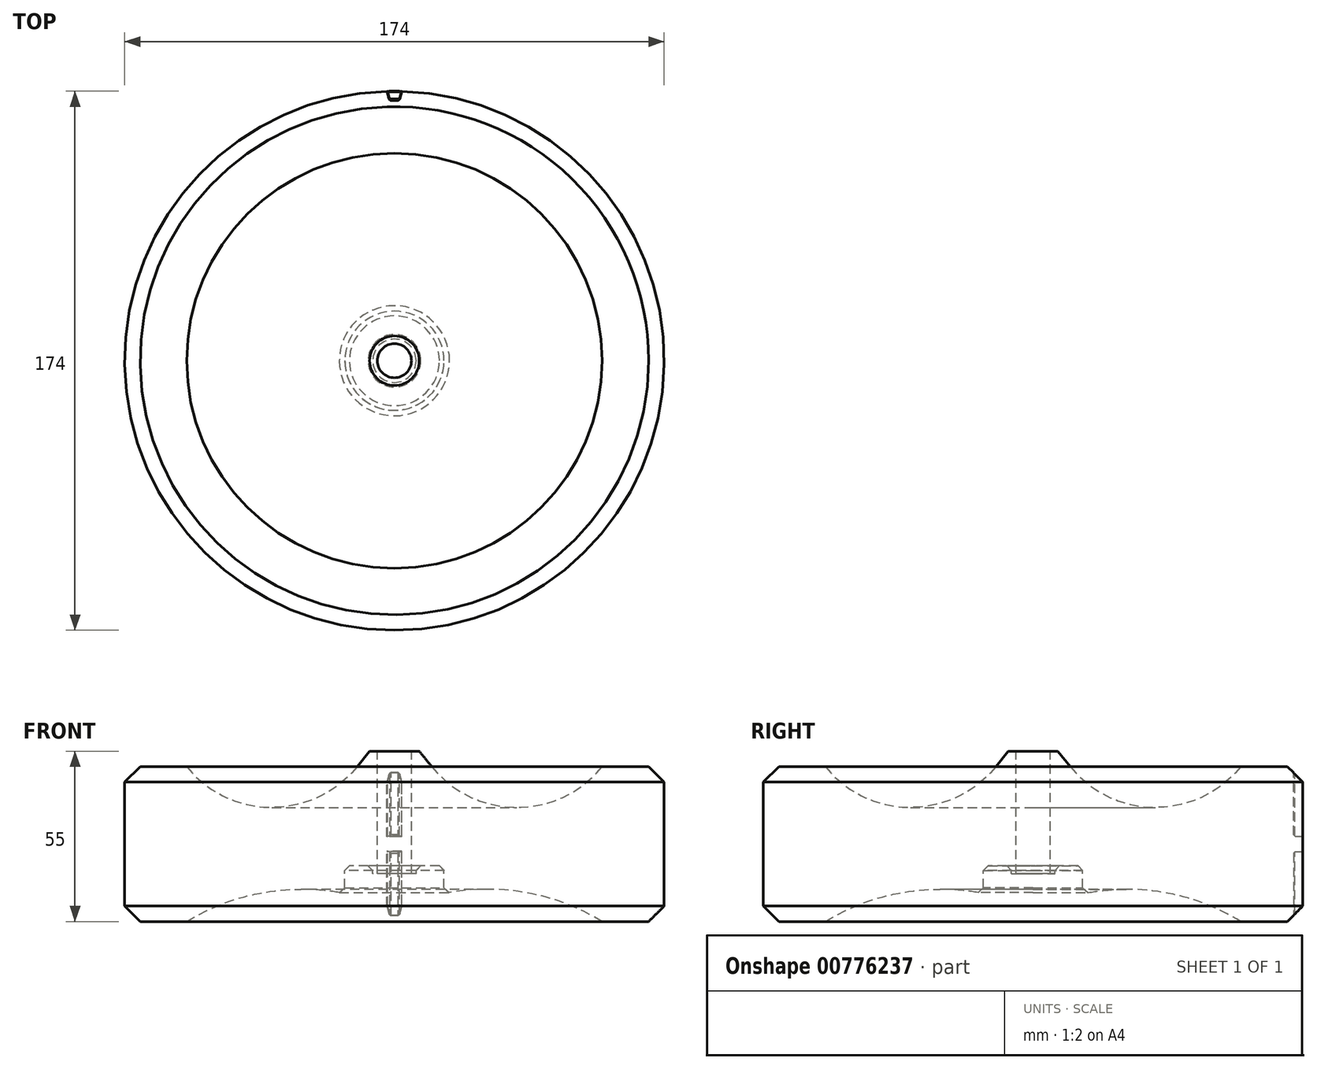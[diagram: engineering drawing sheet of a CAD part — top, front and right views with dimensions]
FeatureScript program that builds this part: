
annotation { "Feature Type Name" : "Feature", "Feature Type Description" : "" }
export const myFeature = defineFeature(function(context is Context, id is Id, definition is map)
    precondition{}
    {
        {
            var Q0;
            Q0=qCreatedBy(makeId("Front.planeOp"),FACE);
            var sketch = newSketch(context, id + "F0", { "sketchPlane" : qUnion([Q0])});
            skLineSegment(sketch, "E0.bottom", {"start": v(0, 0) * mm, "end": v(87, 0) * mm});
            skLineSegment(sketch, "E0.top", {"start": v(0, 50) * mm, "end": v(87, 50) * mm});
            skLineSegment(sketch, "E0.left", {"start": v(0, 0) * mm, "end": v(0, 50) * mm});
            skLineSegment(sketch, "E0.right", {"start": v(87, 0) * mm, "end": v(87, 50) * mm});
            skLineSegment(sketch, "E1", {"start": v(0, 50) * mm, "end": v(0, 55) * mm});
            skLineSegment(sketch, "E2", {"start": v(0, 55) * mm, "end": v(0, 18) * mm});
            skLineSegment(sketch, "E3", {"start": v(0, 18) * mm, "end": v(16, 18) * mm});
            skLineSegment(sketch, "E4", {"start": v(16, 18) * mm, "end": v(16, 0) * mm});
            skLineSegment(sketch, "E5.bottom", {"start": v(0, 55) * mm, "end": v(5.5, 55) * mm});
            skLineSegment(sketch, "E5.top", {"start": v(0, 0) * mm, "end": v(5.5, 0) * mm});
            skLineSegment(sketch, "E5.left", {"start": v(0, 55) * mm, "end": v(0, 0) * mm});
            skLineSegment(sketch, "E5.right", {"start": v(5.5, 55) * mm, "end": v(5.5, 0) * mm});
            skLineSegment(sketch, "E6", {"start": v(5.5, 55) * mm, "end": v(8, 55) * mm});
            skLineSegment(sketch, "E7", {"start": v(8, 55) * mm, "end": v(12.02, 50) * mm});
            skLineSegment(sketch, "E8", {"start": v(0, 18) * mm, "end": v(0, 15.5) * mm});
            skLineSegment(sketch, "E9", {"start": v(0, 15.5) * mm, "end": v(7, 15.5) * mm});
            skLineSegment(sketch, "E10", {"start": v(7, 15.5) * mm, "end": v(7, 18) * mm});
            skLineSegment(sketch, "E11", {"start": v(87, 50) * mm, "end": v(67, 50) * mm});
            skArc(sketch, "E12", {"start": v(12.02, 50) * mm, "mid": v(39.51, 36.84) * mm, "end": v(67, 50) * mm});
            skLineSegment(sketch, "E13", {"start": v(87, 0) * mm, "end": v(67, 0) * mm});
            skArc(sketch, "E14", {"start": v(67, 0) * mm, "mid": v(42.35, 9.34) * mm, "end": v(16, 9) * mm});
            skSolve(sketch);
        }
        {
            var Q0;
            {var subQ0=sQuery(id+"F0.wireOp",EDGE,"E0.right");Q0=makeQuery(id+"F0.imprint","IMPRINT",FACE,{"disambiguationData":[TD([[makeQuery(id+"F0.imprint","IMPRINT",EDGE,{"derivedFrom":subQ0}),1.0]])]});}
            var Q1;
            {var subQ4=sQuery(id+"F0.wireOp",EDGE,"E6");Q1=makeQuery(id+"F0.imprint","IMPRINT",FACE,{"disambiguationData":[TD([[makeQuery(id+"F0.imprint","IMPRINT",EDGE,{"derivedFrom":subQ4}),-1.0]])]});}
            var Q2;
            {var subQ0=sQuery(id+"F0.wireOp",EDGE,"E10");Q2=makeQuery(id+"F0.imprint","IMPRINT",FACE,{"disambiguationData":[TD([[makeQuery(id+"F0.imprint","IMPRINT",EDGE,{"derivedFrom":subQ0}),1.0]])]});}
            var Q3;
            Q3=sQuery(id+"F0.wireOp",EDGE,"E5.left");
            revolve(context, id + "F1", {"surfaceOperationType" : NewSurfaceOperationType.NEW, "entities" : qUnion([Q0, Q1, Q2]), "axis" : qUnion([Q3]), "revolveType" : RevolveType.FULL});
        }
        {
            var Q0;
            Q0=makeQuery(id+"F1.opRevolve","SWEPT_EDGE",EDGE,{"disambiguationData":[OSD([sQuery(id+"F0.wireOp",EDGE,"E0.top"),sQuery(id+"F0.wireOp",EDGE,"E0.right")])]});
            var Q1;
            Q1=makeQuery(id+"F1.opRevolve","SWEPT_EDGE",EDGE,{"disambiguationData":[OSD([sQuery(id+"F0.wireOp",EDGE,"E0.bottom"),sQuery(id+"F0.wireOp",EDGE,"E0.right")])]});
            chamfer(context, id + "F2", {"entities" : qUnion([Q0, Q1]), "width" : 5 * mm, "tangentPropagation" : true});
        }
        {
            var Q0;
            Q0=makeQuery(id+"F1.opRevolve","SWEPT_FACE",FACE,{"disambiguationData":[OSD([sQuery(id+"F0.wireOp",EDGE,"E0.top")])]});
            var sketch = newSketch(context, id + "F3", { "sketchPlane" : qUnion([Q0])});
            skLineSegment(sketch, "E15", {"start": v(0, 0) * mm, "end": v(0, 87) * mm});
            skLineSegment(sketch, "E16.bottom", {"start": v(0, 87) * mm, "end": v(1.5, 87) * mm});
            skLineSegment(sketch, "E16.top", {"start": v(0, 84) * mm, "end": v(1.5, 84) * mm});
            skLineSegment(sketch, "E16.left", {"start": v(0, 87) * mm, "end": v(0, 84) * mm});
            skLineSegment(sketch, "E16.right", {"start": v(1.5, 87) * mm, "end": v(1.5, 84) * mm});
            skLineSegment(sketch, "E17", {"start": v(1.5, 84) * mm, "end": v(2.76, 88.68) * mm});
            skLineSegment(sketch, "E18.MirrorCS", {"start": v(-1.5, 84) * mm, "end": v(-2.76, 88.68) * mm});
            skLineSegment(sketch, "E19.MirrorCS", {"start": v(-1.5, 87) * mm, "end": v(-1.5, 84) * mm});
            skLineSegment(sketch, "E20.MirrorCS", {"start": v(0, 84) * mm, "end": v(-1.5, 84) * mm});
            skLineSegment(sketch, "E21.MirrorCS", {"start": v(0, 87) * mm, "end": v(-1.5, 87) * mm});
            skLineSegment(sketch, "E22", {"start": v(-2.76, 88.68) * mm, "end": v(2.76, 88.68) * mm});
            skSolve(sketch);
        }
        {
            var Q0;
            {var subQ0=sQuery(id+"F3.wireOp",EDGE,"E16.bottom");Q0=makeQuery(id+"F3.imprint","IMPRINT",FACE,{"disambiguationData":[TD([[makeQuery(id+"F3.imprint","IMPRINT",EDGE,{"derivedFrom":subQ0}),-1.0]])]});}
            var Q1;
            {var subQ0=sQuery(id+"F3.wireOp",EDGE,"E21.MirrorCS");Q1=makeQuery(id+"F3.imprint","IMPRINT",FACE,{"disambiguationData":[TD([[makeQuery(id+"F3.imprint","IMPRINT",EDGE,{"derivedFrom":subQ0}),1.0]])]});}
            var Q2;
            {var subQ0=sQuery(id+"F3.wireOp",EDGE,"E16.top");Q2=makeQuery(id+"F3.imprint","IMPRINT",FACE,{"disambiguationData":[TD([[makeQuery(id+"F3.imprint","IMPRINT",EDGE,{"derivedFrom":subQ0}),1.0]])]});}
            var Q3;
            {var subQ0=sQuery(id+"F3.wireOp",EDGE,"E19.MirrorCS");var subQ1=sQuery(id+"F3.wireOp",EDGE,"E18.MirrorCS");var subQ2=makeQuery(id+"F3.imprint","INTERSECT",VERTEX,{"derivedFrom":[subQ1,subQ0,sQuery(id+"F3.wireOp",EDGE,"E20.MirrorCS")]});Q3=makeQuery(id+"F3.imprint","IMPRINT",FACE,{"disambiguationData":[TD([[makeQuery(id+"F3.imprint","IMPRINT",EDGE,{"disambiguationData":[TD([[subQ2,-1.0]])],"derivedFrom":subQ1}),-1.0]])]});}
            var Q4;
            {var subQ0=sQuery(id+"F3.wireOp",EDGE,"E16.left");Q4=makeQuery(id+"F3.imprint","IMPRINT",FACE,{"disambiguationData":[TD([[makeQuery(id+"F3.imprint","IMPRINT",EDGE,{"derivedFrom":subQ0}),-1.0]])]});}
            var Q5;
            {var subQ0=sQuery(id+"F3.wireOp",EDGE,"E17");var subQ1=sQuery(id+"F3.wireOp",EDGE,"E16.right");var subQ2=makeQuery(id+"F3.imprint","INTERSECT",VERTEX,{"derivedFrom":[sQuery(id+"F3.wireOp",EDGE,"E16.top"),subQ1,subQ0]});Q5=makeQuery(id+"F3.imprint","IMPRINT",FACE,{"disambiguationData":[TD([[makeQuery(id+"F3.imprint","IMPRINT",EDGE,{"disambiguationData":[TD([[subQ2,1.0]])],"derivedFrom":subQ1}),1.0]])]});}
            extrude(context, id + "F4", {"entities" : qUnion([Q0, Q1, Q2, Q3, Q4, Q5]), "operationType" : NewBodyOperationType.REMOVE, "oppositeDirection" : true, "depth" : 22.5 * mm, "offsetDistance" : 25 * mm});
        }
        {
            var Q0;
            Q0 = qSketchRegion(id + "F3", true);
            extrude(context, id + "F5", {"entities" : qUnion([Q0]), "operationType" : NewBodyOperationType.REMOVE, "oppositeDirection" : true, "depth" : 75.5 * mm, "offsetDistance" : 25 * mm, "hasSecondDirection" : true, "secondDirectionOppositeDirection" : true, "secondDirectionDepth" : 27.5 * mm});
        }
        {
            var Q0;
            Q0=makeQuery(id+"F4.boolean.opBoolean","COPY",EDGE,{"derivedFrom":makeQuery(id+"F4.opExtrude","CAP_EDGE",EDGE,{"disambiguationData":[OSD([sQuery(id+"F3.wireOp",EDGE,"E16.top"),sQuery(id+"F3.wireOp",EDGE,"E20.MirrorCS")])],"isStart":false})});
            var Q1;
            Q1=makeQuery(id+"F4.boolean.opBoolean","COPY",EDGE,{"derivedFrom":makeQuery(id+"F4.opExtrude","SWEPT_EDGE",EDGE,{"disambiguationData":[OSD([sQuery(id+"F3.wireOp",EDGE,"E16.top"),sQuery(id+"F3.wireOp",EDGE,"E16.right"),sQuery(id+"F3.wireOp",EDGE,"E17")])]})});
            var Q2;
            Q2=makeQuery(id+"F4.boolean.opBoolean","COPY",EDGE,{"derivedFrom":makeQuery(id+"F4.opExtrude","SWEPT_EDGE",EDGE,{"disambiguationData":[OSD([sQuery(id+"F3.wireOp",EDGE,"E18.MirrorCS"),sQuery(id+"F3.wireOp",EDGE,"E19.MirrorCS"),sQuery(id+"F3.wireOp",EDGE,"E20.MirrorCS")])]})});
            var Q3;
            Q3=makeQuery(id+"F5.boolean.opBoolean","COPY",EDGE,{"derivedFrom":makeQuery(id+"F5.opExtrude","SWEPT_EDGE",EDGE,{"disambiguationData":[OSD([sQuery(id+"F3.wireOp",EDGE,"E16.top"),sQuery(id+"F3.wireOp",EDGE,"E16.right"),sQuery(id+"F3.wireOp",EDGE,"E17")])]})});
            var Q4;
            Q4=makeQuery(id+"F5.boolean.opBoolean","COPY",EDGE,{"derivedFrom":makeQuery(id+"F5.opExtrude","SWEPT_EDGE",EDGE,{"disambiguationData":[OSD([sQuery(id+"F3.wireOp",EDGE,"E18.MirrorCS"),sQuery(id+"F3.wireOp",EDGE,"E19.MirrorCS"),sQuery(id+"F3.wireOp",EDGE,"E20.MirrorCS")])]})});
            var Q5;
            Q5=makeQuery(id+"F5.boolean.opBoolean","COPY",EDGE,{"derivedFrom":makeQuery(id+"F5.opExtrude","CAP_EDGE",EDGE,{"disambiguationData":[OSD([sQuery(id+"F3.wireOp",EDGE,"E16.top"),sQuery(id+"F3.wireOp",EDGE,"E20.MirrorCS")])],"isStart":true})});
            chamfer(context, id + "F6", {"entities" : qUnion([Q0, Q1, Q2, Q3, Q4, Q5]), "width" : .5 * mm, "tangentPropagation" : true});
        }
        {
            var Q0;
            Q0=makeQuery(id+"F4.boolean.opBoolean","INTERSECT",EDGE,{"derivedFrom":[makeQuery(id+"F1.opRevolve","SWEPT_FACE",FACE,{"disambiguationData":[OSD([sQuery(id+"F0.wireOp",EDGE,"E0.right")])]}),makeQuery(id+"F4.opExtrude","SWEPT_FACE",FACE,{"disambiguationData":[OSD([sQuery(id+"F3.wireOp",EDGE,"E17")])]})]});
            var Q1;
            Q1=makeQuery(id+"F4.boolean.opBoolean","INTERSECT",EDGE,{"derivedFrom":[makeQuery(id+"F1.opRevolve","SWEPT_FACE",FACE,{"disambiguationData":[OSD([sQuery(id+"F0.wireOp",EDGE,"E0.right")])]}),makeQuery(id+"F4.opExtrude","CAP_FACE",FACE,{"disambiguationData":[OSD([sQuery(id+"F3.wireOp",EDGE,"E16.top"),sQuery(id+"F3.wireOp",EDGE,"E17"),sQuery(id+"F3.wireOp",EDGE,"E18.MirrorCS"),sQuery(id+"F3.wireOp",EDGE,"E20.MirrorCS"),sQuery(id+"F3.wireOp",EDGE,"E22")])],"isStart":false})]});
            var Q2;
            Q2=makeQuery(id+"F4.boolean.opBoolean","INTERSECT",EDGE,{"derivedFrom":[makeQuery(id+"F1.opRevolve","SWEPT_FACE",FACE,{"disambiguationData":[OSD([sQuery(id+"F0.wireOp",EDGE,"E0.right")])]}),makeQuery(id+"F4.opExtrude","SWEPT_FACE",FACE,{"disambiguationData":[OSD([sQuery(id+"F3.wireOp",EDGE,"E18.MirrorCS")])]})]});
            var Q3;
            Q3=makeQuery(id+"F5.boolean.opBoolean","INTERSECT",EDGE,{"derivedFrom":[makeQuery(id+"F1.opRevolve","SWEPT_FACE",FACE,{"disambiguationData":[OSD([sQuery(id+"F0.wireOp",EDGE,"E0.right")])]}),makeQuery(id+"F5.opExtrude","SWEPT_FACE",FACE,{"disambiguationData":[OSD([sQuery(id+"F3.wireOp",EDGE,"E18.MirrorCS")])]})]});
            var Q4;
            Q4=makeQuery(id+"F5.boolean.opBoolean","INTERSECT",EDGE,{"derivedFrom":[makeQuery(id+"F1.opRevolve","SWEPT_FACE",FACE,{"disambiguationData":[OSD([sQuery(id+"F0.wireOp",EDGE,"E0.right")])]}),makeQuery(id+"F5.opExtrude","CAP_FACE",FACE,{"disambiguationData":[OSD([sQuery(id+"F3.wireOp",EDGE,"E16.top"),sQuery(id+"F3.wireOp",EDGE,"E17"),sQuery(id+"F3.wireOp",EDGE,"E18.MirrorCS"),sQuery(id+"F3.wireOp",EDGE,"E20.MirrorCS"),sQuery(id+"F3.wireOp",EDGE,"E22")])],"isStart":true})]});
            var Q5;
            Q5=makeQuery(id+"F5.boolean.opBoolean","INTERSECT",EDGE,{"derivedFrom":[makeQuery(id+"F1.opRevolve","SWEPT_FACE",FACE,{"disambiguationData":[OSD([sQuery(id+"F0.wireOp",EDGE,"E0.right")])]}),makeQuery(id+"F5.opExtrude","SWEPT_FACE",FACE,{"disambiguationData":[OSD([sQuery(id+"F3.wireOp",EDGE,"E17")])]})]});
            var Q6;
            Q6=makeQuery(id+"F4.boolean.opBoolean","INTERSECT",EDGE,{"derivedFrom":[makeQuery(id+"F2.opChamfer","BLEND_FACE",FACE,{"disambiguationData":[OSD([sQuery(id+"F0.wireOp",EDGE,"E0.right"),sQuery(id+"F0.wireOp",EDGE,"E11")])]}),makeQuery(id+"F4.opExtrude","SWEPT_FACE",FACE,{"disambiguationData":[OSD([sQuery(id+"F3.wireOp",EDGE,"E17")])]})]});
            var Q7;
            Q7=makeQuery(id+"F6.opChamfer","BLEND_EDGE",EDGE,{"blendedFrom":[makeQuery(id+"F4.boolean.opBoolean","COPY",EDGE,{"derivedFrom":makeQuery(id+"F4.opExtrude","SWEPT_EDGE",EDGE,{"disambiguationData":[OSD([sQuery(id+"F3.wireOp",EDGE,"E16.top"),sQuery(id+"F3.wireOp",EDGE,"E16.right"),sQuery(id+"F3.wireOp",EDGE,"E17")])]})}),makeQuery(id+"F2.opChamfer","BLEND_FACE",FACE,{"disambiguationData":[OSD([sQuery(id+"F0.wireOp",EDGE,"E0.right"),sQuery(id+"F0.wireOp",EDGE,"E11")])]})],"blendedInto":[makeQuery(id+"F2.opChamfer","BLEND_FACE",FACE,{"disambiguationData":[OSD([sQuery(id+"F0.wireOp",EDGE,"E0.right"),sQuery(id+"F0.wireOp",EDGE,"E11")])]})]});
            var Q8;
            Q8=makeQuery(id+"F4.boolean.opBoolean","INTERSECT",EDGE,{"derivedFrom":[makeQuery(id+"F2.opChamfer","BLEND_FACE",FACE,{"disambiguationData":[OSD([sQuery(id+"F0.wireOp",EDGE,"E0.right"),sQuery(id+"F0.wireOp",EDGE,"E11")])]}),makeQuery(id+"F4.opExtrude","SWEPT_FACE",FACE,{"disambiguationData":[OSD([sQuery(id+"F3.wireOp",EDGE,"E16.top"),sQuery(id+"F3.wireOp",EDGE,"E20.MirrorCS")])]})]});
            var Q9;
            Q9=makeQuery(id+"F6.opChamfer","BLEND_EDGE",EDGE,{"blendedFrom":[makeQuery(id+"F4.boolean.opBoolean","COPY",EDGE,{"derivedFrom":makeQuery(id+"F4.opExtrude","SWEPT_EDGE",EDGE,{"disambiguationData":[OSD([sQuery(id+"F3.wireOp",EDGE,"E18.MirrorCS"),sQuery(id+"F3.wireOp",EDGE,"E19.MirrorCS"),sQuery(id+"F3.wireOp",EDGE,"E20.MirrorCS")])]})}),makeQuery(id+"F2.opChamfer","BLEND_FACE",FACE,{"disambiguationData":[OSD([sQuery(id+"F0.wireOp",EDGE,"E0.right"),sQuery(id+"F0.wireOp",EDGE,"E11")])]})],"blendedInto":[makeQuery(id+"F2.opChamfer","BLEND_FACE",FACE,{"disambiguationData":[OSD([sQuery(id+"F0.wireOp",EDGE,"E0.right"),sQuery(id+"F0.wireOp",EDGE,"E11")])]})]});
            var Q10;
            Q10=makeQuery(id+"F5.boolean.opBoolean","INTERSECT",EDGE,{"derivedFrom":[makeQuery(id+"F2.opChamfer","BLEND_FACE",FACE,{"disambiguationData":[OSD([sQuery(id+"F0.wireOp",EDGE,"E0.right"),sQuery(id+"F0.wireOp",EDGE,"E13")])]}),makeQuery(id+"F5.opExtrude","SWEPT_FACE",FACE,{"disambiguationData":[OSD([sQuery(id+"F3.wireOp",EDGE,"E18.MirrorCS")])]})]});
            var Q11;
            Q11=makeQuery(id+"F6.opChamfer","BLEND_EDGE",EDGE,{"blendedFrom":[makeQuery(id+"F5.boolean.opBoolean","COPY",EDGE,{"derivedFrom":makeQuery(id+"F5.opExtrude","SWEPT_EDGE",EDGE,{"disambiguationData":[OSD([sQuery(id+"F3.wireOp",EDGE,"E18.MirrorCS"),sQuery(id+"F3.wireOp",EDGE,"E19.MirrorCS"),sQuery(id+"F3.wireOp",EDGE,"E20.MirrorCS")])]})}),makeQuery(id+"F2.opChamfer","BLEND_FACE",FACE,{"disambiguationData":[OSD([sQuery(id+"F0.wireOp",EDGE,"E0.right"),sQuery(id+"F0.wireOp",EDGE,"E13")])]})],"blendedInto":[makeQuery(id+"F2.opChamfer","BLEND_FACE",FACE,{"disambiguationData":[OSD([sQuery(id+"F0.wireOp",EDGE,"E0.right"),sQuery(id+"F0.wireOp",EDGE,"E13")])]})]});
            var Q12;
            Q12=makeQuery(id+"F5.boolean.opBoolean","INTERSECT",EDGE,{"derivedFrom":[makeQuery(id+"F2.opChamfer","BLEND_FACE",FACE,{"disambiguationData":[OSD([sQuery(id+"F0.wireOp",EDGE,"E0.right"),sQuery(id+"F0.wireOp",EDGE,"E13")])]}),makeQuery(id+"F5.opExtrude","SWEPT_FACE",FACE,{"disambiguationData":[OSD([sQuery(id+"F3.wireOp",EDGE,"E16.top"),sQuery(id+"F3.wireOp",EDGE,"E20.MirrorCS")])]})]});
            var Q13;
            Q13=makeQuery(id+"F6.opChamfer","BLEND_EDGE",EDGE,{"blendedFrom":[makeQuery(id+"F5.boolean.opBoolean","COPY",EDGE,{"derivedFrom":makeQuery(id+"F5.opExtrude","SWEPT_EDGE",EDGE,{"disambiguationData":[OSD([sQuery(id+"F3.wireOp",EDGE,"E16.top"),sQuery(id+"F3.wireOp",EDGE,"E16.right"),sQuery(id+"F3.wireOp",EDGE,"E17")])]})}),makeQuery(id+"F2.opChamfer","BLEND_FACE",FACE,{"disambiguationData":[OSD([sQuery(id+"F0.wireOp",EDGE,"E0.right"),sQuery(id+"F0.wireOp",EDGE,"E13")])]})],"blendedInto":[makeQuery(id+"F2.opChamfer","BLEND_FACE",FACE,{"disambiguationData":[OSD([sQuery(id+"F0.wireOp",EDGE,"E0.right"),sQuery(id+"F0.wireOp",EDGE,"E13")])]})]});
            var Q14;
            Q14=makeQuery(id+"F5.boolean.opBoolean","INTERSECT",EDGE,{"derivedFrom":[makeQuery(id+"F2.opChamfer","BLEND_FACE",FACE,{"disambiguationData":[OSD([sQuery(id+"F0.wireOp",EDGE,"E0.right"),sQuery(id+"F0.wireOp",EDGE,"E13")])]}),makeQuery(id+"F5.opExtrude","SWEPT_FACE",FACE,{"disambiguationData":[OSD([sQuery(id+"F3.wireOp",EDGE,"E17")])]})]});
            var Q15;
            Q15=makeQuery(id+"F4.boolean.opBoolean","INTERSECT",EDGE,{"derivedFrom":[makeQuery(id+"F2.opChamfer","BLEND_FACE",FACE,{"disambiguationData":[OSD([sQuery(id+"F0.wireOp",EDGE,"E0.right"),sQuery(id+"F0.wireOp",EDGE,"E11")])]}),makeQuery(id+"F4.opExtrude","SWEPT_FACE",FACE,{"disambiguationData":[OSD([sQuery(id+"F3.wireOp",EDGE,"E18.MirrorCS")])]})]});
            chamfer(context, id + "F7", {"entities" : qUnion([Q0, Q1, Q2, Q3, Q4, Q5, Q6, Q7, Q8, Q9, Q10, Q11, Q12, Q13, Q14, Q15]), "width" : .15 * mm, "tangentPropagation" : true});
        }
        {
            var Q0;
            Q0=makeQuery(id+"F1.opRevolve","SWEPT_EDGE",EDGE,{"disambiguationData":[OSD([sQuery(id+"F0.wireOp",EDGE,"E4"),sQuery(id+"F0.wireOp",EDGE,"E14")])]});
            var Q1;
            Q1=makeQuery(id+"F1.opRevolve","SWEPT_EDGE",EDGE,{"disambiguationData":[OSD([sQuery(id+"F0.wireOp",EDGE,"E3"),sQuery(id+"F0.wireOp",EDGE,"E4")])]});
            var Q2;
            Q2=makeQuery(id+"F1.opRevolve","SWEPT_EDGE",EDGE,{"disambiguationData":[OSD([sQuery(id+"F0.wireOp",EDGE,"E3"),sQuery(id+"F0.wireOp",EDGE,"E10")])]});
            chamfer(context, id + "F8", {"entities" : qUnion([Q0, Q1, Q2]), "width" : 1.5 * mm, "tangentPropagation" : true});
        }
    });
